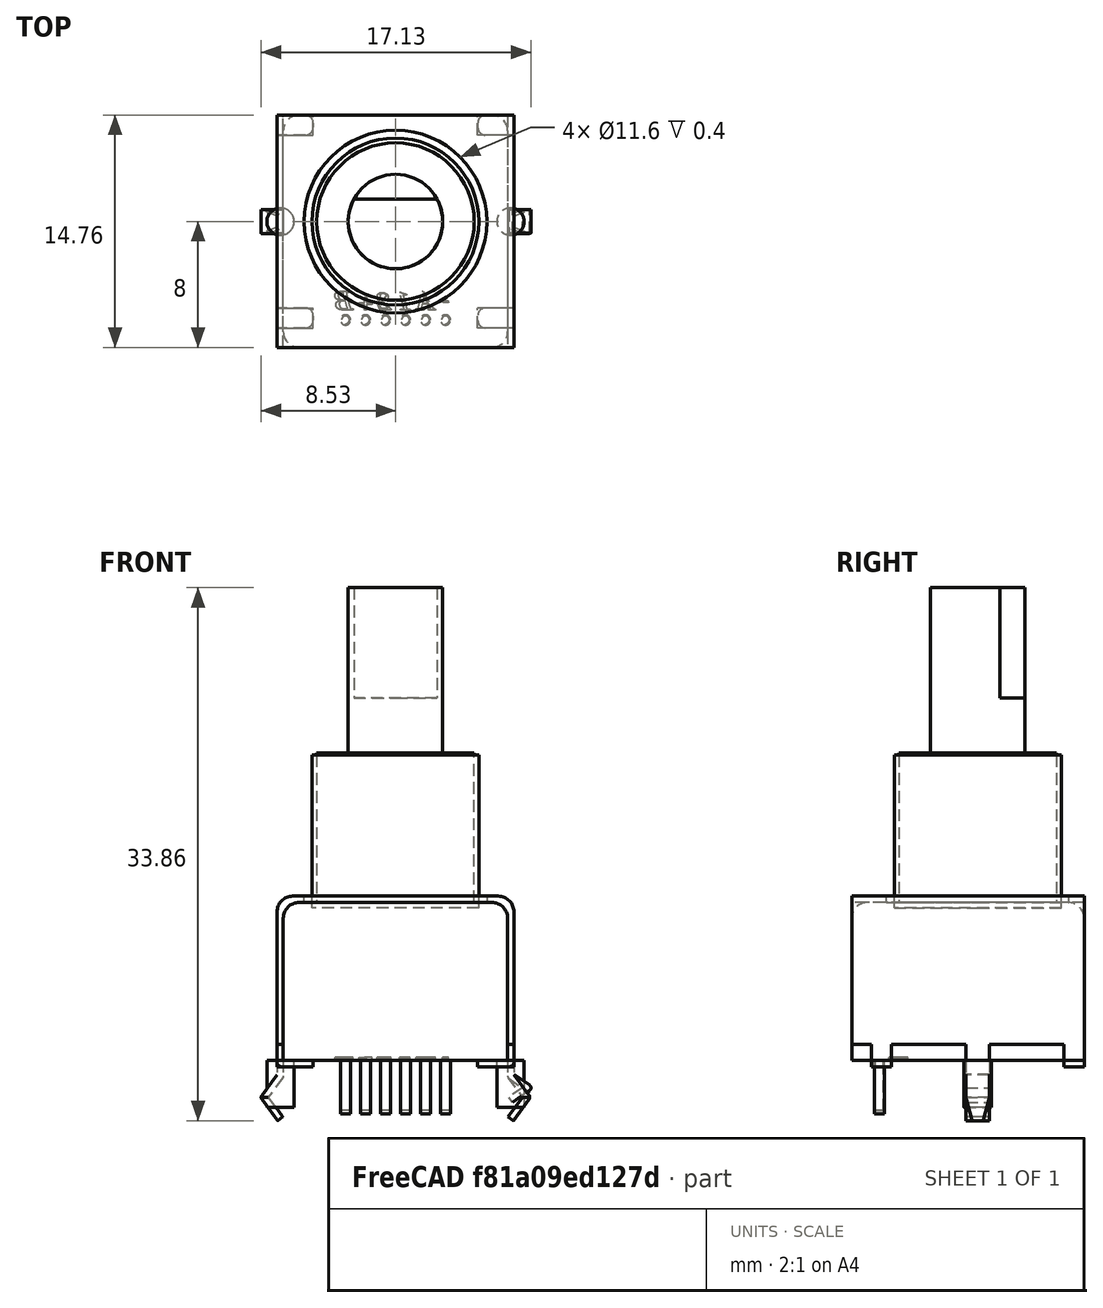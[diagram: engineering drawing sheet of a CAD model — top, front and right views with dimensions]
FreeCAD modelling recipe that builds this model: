
FCSTD DOCUMENT  (FreeCAD 0.17R13335 (Git))
Label: Encoder
License: All rights reserved
LicenseURL: http://en.wikipedia.org/wiki/All_rights_reserved
objects: Sketcher::SketchObject×16, Part::Extrusion×12, Part::Part2DObjectPython×6, Part::Fillet×5, PartDesign::Pad×4, PartDesign::Pocket×4, App::FeaturePython×3, Part::FeaturePython×2, Part::Sweep×2, Part::Cut×2, Part::Mirroring×2, Part::MultiFuse×2, Mesh::Feature×1, Part::Revolution×1, PartDesign::Fillet×1, Part::Feature×1, App::DocumentObjectGroup×1, Part::Compound×1
note: 69 computed .brp shape members not serialized (recipe doc carries the construction recipe); baked Part::Feature solids carry a one-line shape summary decoded from their .brp

FEATURE [Mesh::Feature] _8888  label="EncoderMesh"
  Placement = pos=(0,0,0) rot=(1,0,0;1.5708rad)
FEATURE [Sketcher::SketchObject] Sketch
  MapMode = 5
  Placement = pos=(0,0,0) rot=(1,0,0;1.5708rad)
  sketch-geometry (4):
    g0: LineSegment StartX=5.3 StartY=19.3989 StartZ=0 EndX=0 EndY=19.3989 EndZ=0
    g1: LineSegment StartX=0 StartY=19.3989 StartZ=0 EndX=0 EndY=9.68647 EndZ=0
    g2: LineSegment StartX=0 StartY=9.68647 StartZ=0 EndX=5.3 EndY=9.68647 EndZ=0
    g3: LineSegment StartX=5.3 StartY=9.68647 StartZ=0 EndX=5.3 EndY=19.3989 EndZ=0
  constraints (10):
    c: Coincident(g0,g1)
    c: Coincident(g1,g2)
    c: Coincident(g2,g3)
    c: Coincident(g3,g0)
    c: Horizontal(g0)
    c: Horizontal(g2)
    c: Vertical(g1)
    c: Vertical(g3)
    c: PointOnObject(g0,g-2)
    c: DistanceX(g0,g0) = 5.3
FEATURE [Part::Revolution] Revolve  label="EncoderFPHole"
  Angle = 360
  Axis = (0,0,1)
  Base = (0,0,0)
  Solid = true
  Source = -> Sketch
  Symmetric = false
FEATURE [Sketcher::SketchObject] Sketch001
  MapMode = 5
  sketch-geometry (1):
    g0: Circle CenterX=3.1754 CenterY=-6.24819 CenterZ=0 NormalX=0 NormalY=0 NormalZ=1 AngleXU=0 Radius=0.32
  constraints (1):
    c: Radius(g0) = 0.32
FEATURE [Part::Extrusion] Extrude  label="pcbHole"
  Base = -> Sketch001
  Dir = (0,0,-3.4)
  DirMode = 0
  FaceMakerClass = Part::FaceMakerExtrusion
  LengthFwd = 0
  LengthRev = 0
  Solid = true
  Symmetric = false
FEATURE [Part::FeaturePython] Array  label="EncoderPcbHole"  # Draft array (typed FeaturePython)
  Angle = 360
  ArrayType = 0
  Axis = (0,0,1)
  Base = -> Extrude
  Center = (0,0,0)
  Fuse = false
  IntervalAxis = (0,0,0)
  IntervalX = (-1.27,0,0)
  IntervalY = (0,1,0)
  IntervalZ = (0,0,0)
  NumberPolar = 1
  NumberX = 6
  NumberY = 1
  NumberZ = 1
FEATURE [Sketcher::SketchObject] Sketch002
  MapMode = 5
  sketch-geometry (4):
    g0: LineSegment StartX=-7.125 StartY=6.76 StartZ=0 EndX=7.125 EndY=6.76 EndZ=0
    g1: LineSegment StartX=7.125 StartY=6.76 StartZ=0 EndX=7.125 EndY=-8 EndZ=0
    g2: LineSegment StartX=7.125 StartY=-8 StartZ=0 EndX=-7.125 EndY=-8 EndZ=0
    g3: LineSegment StartX=-7.125 StartY=-8 StartZ=0 EndX=-7.125 EndY=6.76 EndZ=0
  constraints (11):
    c: Coincident(g0,g1)
    c: Coincident(g1,g2)
    c: Coincident(g2,g3)
    c: Coincident(g3,g0)
    c: Horizontal(g2)
    c: Vertical(g1)
    c: Vertical(g3)
    c: DistanceY(g2,g-1) = 8
    c: DistanceY(g3,g3) = 14.76
    c: Symmetric(g0,g0,g-2)
    c: DistanceX(g-1,g0) = 7.125
FEATURE [PartDesign::Pad] Pad
  Length = 10.03
  Length2 = 100
  Profile = -> Sketch002
  Type = 0
FEATURE [PartDesign::Fillet] Fillet  label="Base_"
  Base = -> Pad [Edge5,Edge10,Edge7,Edge4,Edge2,Edge8,Edge12,Edge1]
  Radius = 1
FEATURE [Sketcher::SketchObject] Sketch003
  MapMode = 5
  Placement = pos=(0,0,10.03) rot=(0,0,1;0rad)
  Support = -> [Fillet]
  sketch-geometry (1):
    g0: Circle CenterX=0 CenterY=0 CenterZ=0 NormalX=0 NormalY=0 NormalZ=1 AngleXU=0 Radius=5
  constraints (2):
    c: Coincident(g0,g-1)
    c: Radius(g0) = 5
FEATURE [Part::Extrusion] Extrude001  label="M10"
  Base = -> Sketch003
  Dir = (0,0,9.5)
  DirMode = 0
  FaceMakerClass = Part::FaceMakerExtrusion
  LengthFwd = 0
  LengthRev = 0
  Solid = true
  Symmetric = false
FEATURE [Sketcher::SketchObject] Sketch004
  MapMode = 5
  Placement = pos=(0,0,19.53) rot=(0,0,1;0rad)
  Support = -> [Extrude001]
  sketch-geometry (1):
    g0: Circle CenterX=0 CenterY=0 CenterZ=0 NormalX=0 NormalY=0 NormalZ=1 AngleXU=0 Radius=3
  constraints (2):
    c: Coincident(g0,g-1)
    c: Radius(g0) = 3
FEATURE [Part::Extrusion] Extrude002
  Base = -> Sketch004
  Dir = (0,0,10.5)
  DirMode = 0
  FaceMakerClass = Part::FaceMakerExtrusion
  LengthFwd = 0
  LengthRev = 0
  Solid = true
  Symmetric = false
FEATURE [Sketcher::SketchObject] Sketch005
  ExternalGeometry = -> [Extrude002]
  MapMode = 5
  Placement = pos=(0,0,30.03) rot=(0,0,1;0rad)
  Support = -> [Extrude002]
  sketch-geometry (4):
    g0: LineSegment StartX=-2.64265 StartY=3 StartZ=0 EndX=2.64265 EndY=3 EndZ=0
    g1: LineSegment StartX=2.64265 StartY=3 StartZ=0 EndX=2.64265 EndY=1.42 EndZ=0
    g2: LineSegment StartX=2.64265 StartY=1.42 StartZ=0 EndX=-2.64265 EndY=1.42 EndZ=0
    g3: LineSegment StartX=-2.64265 StartY=1.42 StartZ=0 EndX=-2.64265 EndY=3 EndZ=0
  constraints (12):
    c: Coincident(g0,g1)
    c: Coincident(g1,g2)
    c: Coincident(g2,g3)
    c: Coincident(g3,g0)
    c: Horizontal(g0)
    c: Horizontal(g2)
    c: Vertical(g1)
    c: Vertical(g3)
    c: DistanceY(g-1,g1) = 1.42
    c: Symmetric(g2,g1,g-2)
    c: Tangent(g0,g-3)
    c: PointOnObject(g2,g-3)
FEATURE [PartDesign::Pocket] Pocket  label="Shaft"
  Length = 7
  Length2 = 100
  Profile = -> Sketch005
  Type = 0
FEATURE [Sketcher::SketchObject] Sketch006
  MapMode = 5
  Placement = pos=(0,0,0) rot=(1,0,0;3.14159rad)
  Support = -> [Fillet]
FEATURE [Sketcher::SketchObject] Sketch007
  MapMode = 5
  sketch-geometry (1):
    g0: Circle CenterX=-3.175 CenterY=-6.25 CenterZ=0 NormalX=0 NormalY=0 NormalZ=1 AngleXU=0 Radius=0.25
  constraints (3):
    c: DistanceY(g0,g-1) = 6.25
    c: Radius(g0) = 0.25
    c: DistanceX(g0,g-1) = 3.175
FEATURE [Part::Extrusion] Extrude003  label="pin"
  Base = -> Sketch007
  Dir = (0,0,-3.18)
  DirMode = 0
  FaceMakerClass = Part::FaceMakerExtrusion
  LengthFwd = 0
  LengthRev = 0
  Solid = true
  Symmetric = false
FEATURE [Part::FeaturePython] Array001  label="Pins"  # Draft array (typed FeaturePython)
  Angle = 360
  ArrayType = 0
  Axis = (0,0,1)
  Base = -> Extrude003
  Center = (0,0,0)
  Fuse = false
  IntervalAxis = (0,0,0)
  IntervalX = (1.27,0,0)
  IntervalY = (0,1,0)
  IntervalZ = (0,0,0)
  NumberPolar = 1
  NumberX = 6
  NumberY = 1
  NumberZ = 1
FEATURE [Sketcher::SketchObject] Sketch008
  MapMode = 5
  Placement = pos=(0,0,0) rot=(1,0,0;1.5708rad)
  sketch-geometry (4):
    g0: LineSegment StartX=7.305 StartY=0 StartZ=0 EndX=7.305 EndY=-1 EndZ=0
    g1: LineSegment StartX=7.305 StartY=-1 StartZ=0 EndX=8.305 EndY=-2.35 EndZ=0
    g2: LineSegment StartX=8.305 StartY=-2.35 StartZ=0 EndX=7.305 EndY=-3.7 EndZ=0
    g3: LineSegment [constr] StartX=7.305 StartY=-1 StartZ=0 EndX=7.305 EndY=-4.57005 EndZ=0
  constraints (12):
    c: PointOnObject(g0,g-1)
    c: Vertical(g0)
    c: Coincident(g0,g1)
    c: Coincident(g1,g2)
    c: DistanceY(g0,g-1) = 1
    c: DistanceX(g-1,g0) = 7.305
    c: DistanceY(g2,g-1) = 3.7
    c: Coincident(g3,g0)
    c: Vertical(g3)
    c: PointOnObject(g2,g3)
    c: Equal(g1,g2)
    c: DistanceX(g0,g1) = 1
FEATURE [Part::Feature] Face
  Placement = pos=(0.015,0,0) rot=(0,0,1;0rad)
  shape: bbox 0.4 x 1.5 x 2e-07 mm, 1 faces, 0 solids (baked)
FEATURE [Part::Sweep] Sweep
  Frenet = false
  Sections = -> [Face]
  Solid = true
  Transition = 2
FEATURE [App::FeaturePython] Dimension  # Draft dimension (typed FeaturePython)
  Dimline = (22.7622,7.51765,0)
  Direction = (0,0,0)
  Distance = 14.76
  End = (6.125,6.76,0)
  Normal = (0,0,1)
  Start = (6.125,-8,0)
FEATURE [App::FeaturePython] Dimension001  # Draft dimension (typed FeaturePython)
  Dimline = (7.12058,-16.8852,0)
  Direction = (0,0,0)
  Distance = 14.25
  End = (7.125,-7,0)
  Normal = (0,0,1)
  Start = (-7.125,-7,0)
FEATURE [App::FeaturePython] Dimension002  # Draft dimension (typed FeaturePython)
  Dimline = (-16.7982,0,14.4985)
  Direction = (0,0,0)
  Distance = 10.03
  End = (-7.125,-0.62,0)
  Normal = (0,1,0)
  Start = (-7.125,-0.62,10.03)
FEATURE [Sketcher::SketchObject] Sketch009
  MapMode = 5
  sketch-geometry (4):
    g0: LineSegment StartX=-7.525 StartY=6.76 StartZ=0 EndX=7.525 EndY=6.76 EndZ=0
    g1: LineSegment StartX=7.525 StartY=6.76 StartZ=0 EndX=7.525 EndY=-8 EndZ=0
    g2: LineSegment StartX=7.525 StartY=-8 StartZ=0 EndX=-7.525 EndY=-8 EndZ=0
    g3: LineSegment StartX=-7.525 StartY=-8 StartZ=0 EndX=-7.525 EndY=6.76 EndZ=0
  constraints (11):
    c: Coincident(g0,g1)
    c: Coincident(g1,g2)
    c: Coincident(g2,g3)
    c: Coincident(g3,g0)
    c: Horizontal(g2)
    c: Vertical(g1)
    c: Vertical(g3)
    c: DistanceY(g2,g-1) = 8
    c: DistanceY(g3,g3) = 14.76
    c: Symmetric(g0,g0,g-2)
    c: DistanceX(g-1,g0) = 7.525
FEATURE [Part::Extrusion] Extrude004
  Base = -> Sketch009
  Dir = (0,0,10.43)
  DirMode = 0
  FaceMakerClass = Part::FaceMakerExtrusion
  LengthFwd = 0
  LengthRev = 0
  Solid = true
  Symmetric = false
FEATURE [PartDesign::Pad] Pad001
  Length = 10.03
  Length2 = 100
  Profile = -> Sketch002
  Type = 0
FEATURE [Part::Fillet] Fillet001
  Base = -> Pad001
  Edges = 2 edges r=1: [Edge7,Edge12]
FEATURE [Part::Cut] Cut
  Base = -> Extrude004
  Tool = -> Fillet001
FEATURE [Part::Fillet] Fillet002
  Base = -> Cut
  Edges = 2 edges r=1: [Edge27,Edge29]
FEATURE [Sketcher::SketchObject] Sketch011
  MapMode = 5
  Placement = pos=(0,0,10.43) rot=(0,0,1;0rad)
  Support = -> [Fillet002]
  sketch-geometry (1):
    g0: Circle CenterX=0 CenterY=0 CenterZ=0 NormalX=0 NormalY=0 NormalZ=1 AngleXU=0 Radius=5.8
  constraints (2):
    c: Coincident(g0,g-1)
    c: Radius(g0) = 5.8
FEATURE [PartDesign::Pocket] Pocket002
  Length = 5
  Length2 = 100
  Profile = -> Sketch011
  Type = 1
FEATURE [Sketcher::SketchObject] Sketch012
  ExternalGeometry = -> [Pocket002]
  MapMode = 5
  Placement = pos=(7.525,0,0) rot=(0.57735,0.57735,0.57735;2.0944rad)
  Support = -> [Pocket002]
  sketch-geometry (8):
    g0: LineSegment StartX=5.49 StartY=0 StartZ=0 EndX=6.76 EndY=0 EndZ=0
    g1: LineSegment StartX=6.76 StartY=0 StartZ=0 EndX=6.76 EndY=-0.4 EndZ=0
    g2: LineSegment StartX=6.76 StartY=-0.4 StartZ=0 EndX=5.49 EndY=-0.4 EndZ=0
    g3: LineSegment StartX=5.49 StartY=-0.4 StartZ=0 EndX=5.49 EndY=0 EndZ=0
    g4: LineSegment StartX=-6.76 StartY=0 StartZ=0 EndX=-5.49 EndY=0 EndZ=0
    g5: LineSegment StartX=-5.49 StartY=0 StartZ=0 EndX=-5.49 EndY=-0.4 EndZ=0
    g6: LineSegment StartX=-5.49 StartY=-0.4 StartZ=0 EndX=-6.76 EndY=-0.4 EndZ=0
    g7: LineSegment StartX=-6.76 StartY=-0.4 StartZ=0 EndX=-6.76 EndY=0 EndZ=0
  constraints (23):
    c: Coincident(g0,g1)
    c: Coincident(g1,g2)
    c: Coincident(g2,g3)
    c: Coincident(g3,g0)
    c: Horizontal(g0)
    c: Horizontal(g2)
    c: Vertical(g1)
    c: Vertical(g3)
    c: DistanceX(g2,g2) = 1.27
    c: DistanceY(g3,g3) = 0.4
    c: Coincident(g0,g-3)
    c: Coincident(g4,g5)
    c: Coincident(g5,g6)
    c: Coincident(g6,g7)
    c: Coincident(g7,g4)
    c: Horizontal(g4)
    c: Horizontal(g6)
    c: Vertical(g5)
    c: Vertical(g7)
    c: Equal(g6,g2)
    c: Equal(g5,g3)
    c: PointOnObject(g4,g-3)
    c: Symmetric(g2,g5,g-2)
FEATURE [PartDesign::Pad] Pad002
  Length = 2.3
  Length2 = 100
  Profile = -> Sketch012
  Reversed = true
  Type = 0
FEATURE [Sketcher::SketchObject] Sketch013
  ExternalGeometry = -> [Pad002]
  MapMode = 5
  Placement = pos=(-7.525,0,0) rot=(0.57735,-0.57735,-0.57735;2.0944rad)
  Support = -> [Pad002]
  sketch-geometry (8):
    g0: LineSegment StartX=-6.76 StartY=0 StartZ=0 EndX=-5.49 EndY=0 EndZ=0
    g1: LineSegment StartX=-5.49 StartY=0 StartZ=0 EndX=-5.49 EndY=-0.4 EndZ=0
    g2: LineSegment StartX=-5.49 StartY=-0.4 StartZ=0 EndX=-6.76 EndY=-0.4 EndZ=0
    g3: LineSegment StartX=-6.76 StartY=-0.4 StartZ=0 EndX=-6.76 EndY=0 EndZ=0
    g4: LineSegment StartX=5.49 StartY=-0.4 StartZ=0 EndX=6.76 EndY=-0.4 EndZ=0
    g5: LineSegment StartX=6.76 StartY=-0.4 StartZ=0 EndX=6.76 EndY=0 EndZ=0
    g6: LineSegment StartX=6.76 StartY=0 StartZ=0 EndX=5.49 EndY=0 EndZ=0
    g7: LineSegment StartX=5.49 StartY=0 StartZ=0 EndX=5.49 EndY=-0.4 EndZ=0
  constraints (20):
    c: Coincident(g0,g1)
    c: Coincident(g1,g2)
    c: Coincident(g2,g3)
    c: Coincident(g3,g0)
    c: Horizontal(g0)
    c: Horizontal(g2)
    c: Vertical(g1)
    c: Vertical(g3)
    c: Coincident(g0,g-3)
    c: Coincident(g1,g-4)
    c: Coincident(g4,g5)
    c: Coincident(g5,g6)
    c: Coincident(g6,g7)
    c: Coincident(g7,g4)
    c: Horizontal(g4)
    c: Horizontal(g6)
    c: Vertical(g5)
    c: Vertical(g7)
    c: Coincident(g4,g-5)
    c: Coincident(g5,g-6)
FEATURE [PartDesign::Pad] Pad003
  Length = 2.3
  Length2 = 100
  Profile = -> Sketch013
  Reversed = true
  Type = 0
FEATURE [Sketcher::SketchObject] Sketch014  label="MountingBracketHoles"
  MapMode = 5
  Placement = pos=(7.525,0,0) rot=(0.57735,0.57735,0.57735;2.0944rad)
  Support = -> [Pad003]
  sketch-geometry (12):
    g0: LineSegment StartX=-8 StartY=0 StartZ=0 EndX=-6.76 EndY=0 EndZ=0
    g1: LineSegment StartX=-6.76 StartY=0 StartZ=0 EndX=-6.76 EndY=1 EndZ=0
    g2: LineSegment StartX=-6.76 StartY=1 StartZ=0 EndX=-8 EndY=1 EndZ=0
    g3: LineSegment StartX=-8 StartY=1 StartZ=0 EndX=-8 EndY=0 EndZ=0
    g4: LineSegment StartX=-5.49 StartY=0 StartZ=0 EndX=-0.75 EndY=0 EndZ=0
    g5: LineSegment StartX=-0.75 StartY=0 StartZ=0 EndX=-0.75 EndY=1 EndZ=0
    g6: LineSegment StartX=-0.75 StartY=1 StartZ=0 EndX=-5.49 EndY=1 EndZ=0
    g7: LineSegment StartX=-5.49 StartY=1 StartZ=0 EndX=-5.49 EndY=0 EndZ=0
    g8: LineSegment StartX=0.75 StartY=0 StartZ=0 EndX=5.49 EndY=0 EndZ=0
    g9: LineSegment StartX=5.49 StartY=0 StartZ=0 EndX=5.49 EndY=1 EndZ=0
    g10: LineSegment StartX=5.49 StartY=1 StartZ=0 EndX=0.75 EndY=1 EndZ=0
    g11: LineSegment StartX=0.75 StartY=1 StartZ=0 EndX=0.75 EndY=0 EndZ=0
  constraints (27):
    c: Coincident(g0,g1)
    c: Coincident(g1,g2)
    c: Coincident(g2,g3)
    c: Coincident(g3,g0)
    c: Horizontal(g0)
    c: Horizontal(g2)
    c: Vertical(g1)
    c: Vertical(g3)
    c: DistanceY(g1,g1) = 1
    c: Coincident(g4,g5)
    c: Coincident(g5,g6)
    c: Coincident(g6,g7)
    c: Coincident(g7,g4)
    c: Horizontal(g4)
    c: Horizontal(g6)
    c: Vertical(g5)
    c: Vertical(g7)
    c: Equal(g7,g1)
    c: Coincident(g8,g9)
    c: Coincident(g9,g10)
    c: Coincident(g10,g11)
    c: Coincident(g11,g8)
    c: Horizontal(g8)
    c: Horizontal(g10)
    c: Vertical(g9)
    c: Vertical(g11)
    c: Equal(g5,g11)
FEATURE [Part::Sweep] Sweep001
  Frenet = false
  Placement = pos=(0,0,0) rot=(0.476874,-0.135041,-0.868536;0.000912rad)
  Sections = -> [Face]
  Solid = true
  Spine = -> Sketch008 [Edge1,Edge2,Edge3]
  Transition = 2
FEATURE [Sketcher::SketchObject] Sketch015
  ExternalGeometry = -> [Sweep001]
  MapMode = 5
  Placement = pos=(7.125,-0.00564224,0.000876003) rot=(-0.577153,0.577359,0.577539;4.18801rad)
  Support = -> [Sweep001]
  sketch-geometry (6):
    g0: LineSegment StartX=0.75 StartY=-2.35 StartZ=0 EndX=0.75 EndY=-3.83095 EndZ=0
    g1: LineSegment StartX=0.75 StartY=-3.83095 StartZ=0 EndX=0.342924 EndY=-3.83095 EndZ=0
    g2: LineSegment StartX=0.342924 StartY=-3.83095 StartZ=0 EndX=0.75 EndY=-2.35 EndZ=0
    g3: LineSegment StartX=-0.75 StartY=-3.83095 StartZ=0 EndX=-0.342924 EndY=-3.83095 EndZ=0
    g4: LineSegment StartX=-0.342924 StartY=-3.83095 StartZ=0 EndX=-0.75 EndY=-2.35 EndZ=0
    g5: LineSegment StartX=-0.75 StartY=-2.35 StartZ=0 EndX=-0.75 EndY=-3.83095 EndZ=0
  constraints (13):
    c: Coincident(g-3,g0)
    c: Coincident(g0,g-4)
    c: Coincident(g0,g1)
    c: Horizontal(g1)
    c: Coincident(g1,g2)
    c: Coincident(g2,g0)
    c: Coincident(g-4,g3)
    c: PointOnObject(g3,g-4)
    c: Coincident(g3,g4)
    c: Coincident(g4,g-3)
    c: Coincident(g4,g5)
    c: Coincident(g5,g3)
    c: Symmetric(g3,g1,g-2)
FEATURE [PartDesign::Pocket] Pocket004
  Length = 5
  Length2 = 100
  Placement = pos=(0,0,0) rot=(0.476874,-0.135041,-0.868536;0.000912rad)
  Profile = -> Sketch015
  Type = 1
FEATURE [PartDesign::Pocket] Pocket005
  Length = 5
  Length2 = 100
  Profile = -> Sketch014
  Type = 1
FEATURE [Part::Fillet] Fillet003  label="MountBracketPin"
  Base = -> Pocket004
  Edges = 2 edges r=0.1: [Edge27,Edge40]
FEATURE [Part::Mirroring] Part__Mirroring  label="MountBracketPin (Mirror #1)"
  Base = (0,0,0)
  Normal = (1,0,0)
  Source = -> Fillet003
FEATURE [Part::Fillet] Fillet004  label="MountBracketBody"
  Base = -> Pocket005
  Edges = 8 edges r=0.5: [Edge43,Edge74,Edge108,Edge129,Edge135,Edge137,Edge140,Edge143]
FEATURE [Part::MultiFuse] Fusion  label="MountBracket_"
  Shapes = -> [Part__Mirroring,Fillet003,Fillet004]
FEATURE [Part::Fillet] Fillet005  label="MountBracket"
  Base = -> Fusion
  Edges = 4 edges r=0.3: [Edge98,Edge107,Edge220,Edge223]
FEATURE [App::DocumentObjectGroup] Group  label="Dimensions"
  Group = -> [Dimension,Dimension001,Dimension002]
FEATURE [Sketcher::SketchObject] Sketch016
  MapMode = 5
  Placement = pos=(0,0,0) rot=(1,0,0;3.14159rad)
  sketch-geometry (1):
    g0: Circle CenterX=7.305 CenterY=0 CenterZ=0 NormalX=0 NormalY=0 NormalZ=1 AngleXU=0 Radius=0.865
  constraints (3):
    c: PointOnObject(g0,g-1)
    c: DistanceX(g-1,g0) = 7.305
    c: Radius(g0) = 0.865
FEATURE [Part::Extrusion] Extrude005
  Base = -> Sketch016
  Dir = (0,0,-3)
  DirMode = 0
  FaceMakerClass = Part::FaceMakerExtrusion
  LengthFwd = 0
  LengthRev = 0
  Solid = true
  Symmetric = false
FEATURE [Part::Mirroring] Part__Mirroring001  label="Extrude005 (Mirror #2)"
  Base = (0,0,0)
  Normal = (1,0,0)
  Source = -> Extrude005
FEATURE [Part::Compound] Compound001  label="EncoderPcbHolesWIthMountBracket"
  Links = -> [Part__Mirroring001,Extrude005,Array]
FEATURE [Part::Part2DObjectPython] ShapeString  # Draft 2D object (typed FeaturePython)
  FontFile = <path>
  Placement = pos=(3.41915,-5.4626,0) rot=(0,1,0;3.14159rad)
  Size = 0.7
  String = -
  Tracking = 0
FEATURE [Part::Part2DObjectPython] ShapeString001  # Draft 2D object (typed FeaturePython)
  FontFile = <path>
  Placement = pos=(2.39713,-5.61633,0) rot=(0,1,0;3.14159rad)
  Size = 0.7
  String = A
  Tracking = 0
FEATURE [Part::Part2DObjectPython] ShapeString002  # Draft 2D object (typed FeaturePython)
  FontFile = <path>
  Placement = pos=(1.0136,-5.62508,0) rot=(0,1,0;3.14159rad)
  Size = 0.7
  String = 1
  Tracking = 0
FEATURE [Part::Part2DObjectPython] ShapeString003  # Draft 2D object (typed FeaturePython)
  FontFile = <path>
  Placement = pos=(-0.346103,-5.62289,0) rot=(0,1,0;3.14159rad)
  Size = 0.7
  String = 2
  Tracking = 0
FEATURE [Part::Part2DObjectPython] ShapeString004  # Draft 2D object (typed FeaturePython)
  FontFile = <path>
  Placement = pos=(-1.41927,-5.61723,0) rot=(0,1,0;3.14159rad)
  Size = 0.7
  String = +
  Tracking = 0
FEATURE [Part::Part2DObjectPython] ShapeString005  # Draft 2D object (typed FeaturePython)
  FontFile = <path>
  Placement = pos=(-2.76356,-5.61606,0) rot=(0,1,0;3.14159rad)
  Size = 0.7
  String = B
  Tracking = 0
FEATURE [Part::Extrusion] Extrude006
  Base = -> ShapeString
  Dir = (0,0,0.2)
  DirMode = 0
  FaceMakerClass = Part::FaceMakerExtrusion
  LengthFwd = 0
  LengthRev = 0
  Solid = true
  Symmetric = false
FEATURE [Part::Extrusion] Extrude007
  Base = -> ShapeString001
  Dir = (0,0,0.2)
  DirMode = 0
  FaceMakerClass = Part::FaceMakerExtrusion
  LengthFwd = 0
  LengthRev = 0
  Solid = true
  Symmetric = false
FEATURE [Part::Extrusion] Extrude008
  Base = -> ShapeString002
  Dir = (0,0,0.2)
  DirMode = 0
  FaceMakerClass = Part::FaceMakerExtrusion
  LengthFwd = 0
  LengthRev = 0
  Solid = true
  Symmetric = false
FEATURE [Part::Extrusion] Extrude009
  Base = -> ShapeString003
  Dir = (0,0,0.2)
  DirMode = 0
  FaceMakerClass = Part::FaceMakerExtrusion
  LengthFwd = 0
  LengthRev = 0
  Solid = true
  Symmetric = false
FEATURE [Part::Extrusion] Extrude010
  Base = -> ShapeString004
  Dir = (0,0,0.2)
  DirMode = 0
  FaceMakerClass = Part::FaceMakerExtrusion
  LengthFwd = 0
  LengthRev = 0
  Solid = true
  Symmetric = false
FEATURE [Part::Extrusion] Extrude011
  Base = -> ShapeString005
  Dir = (0,0,0.2)
  DirMode = 0
  FaceMakerClass = Part::FaceMakerExtrusion
  LengthFwd = 0
  LengthRev = 0
  Solid = true
  Symmetric = false
FEATURE [Part::MultiFuse] Fusion001  label="PinMarks"
  Shapes = -> [Extrude006,Extrude007,Extrude008,Extrude009,Extrude010,Extrude011]
FEATURE [Part::Cut] Cut001  label="Base"
  Base = -> Fillet
  Tool = -> Fusion001
note: 6 file-system paths scrubbed to <path> (originals preserved in the JSON sidecar)
